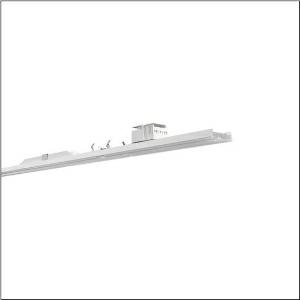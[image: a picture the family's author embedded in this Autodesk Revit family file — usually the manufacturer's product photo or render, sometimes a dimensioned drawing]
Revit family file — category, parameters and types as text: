
# Revit family: licross_r__11_recessed_mo_51tl1e7n48xf_578a
name_source: partatom
category: Lighting Fixtures
units: mm (PartAtom-declared; Revit-internal decimal feet)

## family parameters
Cut with Voids When Loaded = No
Host = Face
Light Source = No
Part Type = Normal
Room Calculation Point = No
Round Connector Dimension = Use Diameter
Shared = No

## types (1)
- Licross® 11 Recessed MO (1 x LED, 8090 lm, 47.6 W, 4000K)
    Apparent Load = 48 VA
    CIE Flux Codes = 85 95 99 100 100
    Color Rendering = 80
    Color Temperature = 4000K
    Default Elevation = 1800 mm
    Description = Licross® 11 Recessed MO, luminaire insert, of sheet steel, galvanised, coil coated, white, length: 1.500mm, width: 66mm, height: 67mm, LED rated luminous flux: 8.090lm, light colour: 840, control gear: ON/OFF, control gear: ECG, with plug, 3-pole, with phase selection, mains connection: 220..240V, AC, 50/60Hz, halogen-free wiring, primary optical cover: cover, of PMMA, light emission: direct distribution, protection rating (complete): IP40, insulation class (complete): insulation class I (protective earthing), certification: CE, ENEC, VDE, UKCA, protection symbol: D if used in an environment without relevant dust loads with corresponding accessories, permissible ambient temperature for indoor applications: -35..+40°C, reducing of maximum allowable ambient temperature of 5°C with ceiling mounting, corresponds to IFS (International Featured Standards) requirements for safety and quality in the food industry, LABS conformity tested according to VDMA 24364:2018-05, packaging unit: 1 piece
    Height = 58 mm
    Lamp = 1 x LED
    Lamp Light Flux = 8090 lm
    Lamp Power = 47.6 W
    Lamp count = 1
    Length = 1500 mm
    Luminous efficacy = 170 lm/W
    Manufacturer = Siteco
    ModVariant = No
    Model = 51TL1E7N48XF
    Mounting Place = Ceiling
    Mounting Type = Pendant
    Number of Poles = 1
    OnlyDefault = Yes
    Power Factor = 1
    Product Name = Licross® 11 Recessed MO
    Product group = luminaire insert
    ProductGroupID = 902
    Protection Class = Protection class I
    Protection Degree = IP 40
    RLX_Detail_Level = 1
    RlxData = <blob elided: 18957 chars, md5=c2d56af5>
    Socket = socket
    Standby Power = 0 W
    System Light Flux = 8090 lm
    System Power = 48 W
    Type Comments = Product without accessories
    Type Image = l_1266722.jpg
    URL = http://relux.com
    VarID = ---
    Voltage = 0 V
    Weight = 0.00 kg
    Width = 66 mm

## geometry (parser evidence)
native form markers: Blend x4, Sweep x11
no freeform markers — native parametric forms only
